# Revit family: Haworth_BuzziSpark_LoungeChair_AP_PRELIMINARY
name_source: partatom
category: Furniture
revit_build: Autodesk Revit 2018 (Build: 20170223_1515(x64)
units: mm (PartAtom-declared; Revit-internal decimal feet)

## family parameters
Always vertical = Yes
Cut with Voids When Loaded = No
OmniClass Number = 23.40.70.14.64.21
OmniClass Title = Systems Furniture
Room Calculation Point = No
Shared = No
Work Plane-Based = No

## types (3) — shared parameters
Actual Depth = 953 mm
Actual Width = 1313 mm
Arm Offset = 140 mm
Assembly Code = E2020200
Back Cushion Width = 903 mm
Back Upholstery Width = 1085 mm
Description = Haworth - BuzziSpark - Lounge Chair
Left Tablet = Yes
Manufacturer = Haworth
Middle Leg Control = No
Model = Sofa AG 111
Revision Number = 1
Right Tablet = Yes
Seat Depth = 700 mm
Seat Height = 450 mm
Seat Width = 860 mm
Side Upholstery Width = 648 mm
Size = Verify Final Dim. w/ Haworth
URL = https://www.haworth.com
URL - Product = https://www.haworth.com
Warranty = http://www.haworth.com
With Arm Cushion = Yes

## per-type parameters (varying)
| type | Actual Height | High Back | Low Back |
| High Back | 1653 mm | Yes | No |
| Medium Back | 1388 mm | No | No |
| Low Back | 1388 mm | No | Yes |

type visibility flags (boolean, named after types; folded from table):
- High Back: Yes: (none)
- Medium Back: Yes: Medium Back
- Low Back: Yes: (none)

## geometry (parser evidence)
native form markers: Extrusion x2, Sweep x17
no freeform markers — native parametric forms only
